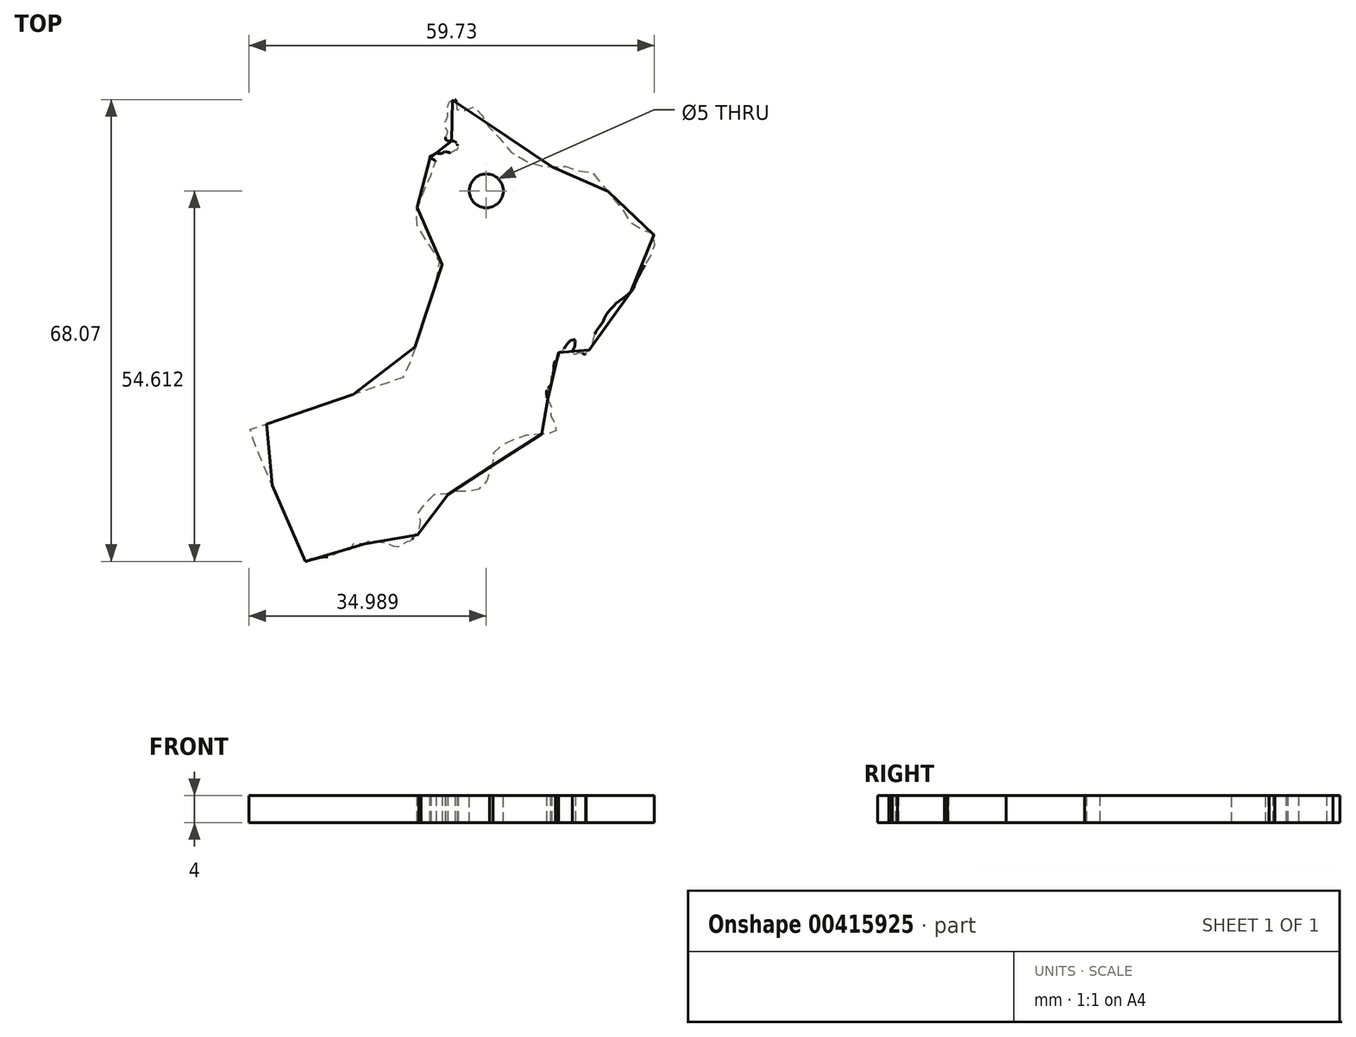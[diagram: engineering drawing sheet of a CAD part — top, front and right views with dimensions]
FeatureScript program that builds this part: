
annotation { "Feature Type Name" : "Feature", "Feature Type Description" : "" }
export const myFeature = defineFeature(function(context is Context, id is Id, definition is map)
    precondition{}
    {
        {
            var Q0;
            Q0=qCreatedBy(makeId("Top.planeOp"),FACE);
            var sketch = newSketch(context, id + "F0", { "sketchPlane" : qUnion([Q0])});
            skLineSegment(sketch, "E0", {"start": v(29.6, 33.78) * mm, "end": v(-30.4, -34.67) * mm, "construction": true});
            skPoint(sketch, "E1.287.internal.snap0", {"position": v(-0.4, -34.67) * mm});
            skFitSpline(sketch, "E1", {"points": [v(-21.86, -34.42) * mm, v(-22.26, -33.64) * mm, v(-22.63, -32.67) * mm, v(-23.08, -31.68) * mm, v(-23.6, -30.58) * mm, v(-23.98, -29.63) * mm, v(-24.43, -28.6) * mm, v(-24.98, -27.36) * mm, v(-25.63, -25.87) * mm, v(-25.94, -25.15) * mm, v(-26.4, -24.13) * mm, v(-26.85, -23.03) * mm, v(-27.5, -21.52) * mm, v(-27.88, -20.6) * mm, v(-28.48, -19.3) * mm, v(-28.76, -18.7) * mm, v(-29.17, -17.66) * mm, v(-29.58, -16.67) * mm, v(-29.95, -15.84) * mm, v(-30.23, -15.24) * mm, v(-30.16, -15.04) * mm, v(-29.37, -14.8) * mm, v(-28.12, -14.41) * mm, v(-27.2, -14.05) * mm, v(-25.85, -13.6) * mm, v(-25.24, -13.39) * mm, v(-23.99, -12.96) * mm, v(-23.02, -12.68) * mm, v(-21.7, -12.18) * mm, v(-20.03, -11.61) * mm, v(-18.68, -11.14) * mm, v(-17.36, -10.67) * mm, v(-15.5, -10.04) * mm, v(-14.32, -9.6) * mm, v(-12.78, -9.1) * mm, v(-11.22, -8.54) * mm, v(-10.12, -8.17) * mm, v(-8.72, -7.66) * mm, v(-7.5, -7.3) * mm, v(-7.05, -7.07) * mm, v(-6.8, -6.26) * mm, v(-6.51, -5.37) * mm, v(-6.2, -4.43) * mm, v(-5.8, -3) * mm, v(-5.36, -1.8) * mm, v(-4.98, -0.7) * mm, v(-4.86, -0.22) * mm, v(-4.67, 0.33) * mm, v(-4.07, 2.12) * mm, v(-3.53, 3.76) * mm, v(-3.2, 5) * mm, v(-2.82, 6.07) * mm, v(-2.13, 8.22) * mm, v(-1.83, 8.96) * mm, v(-1.76, 9.23) * mm, v(-2.13, 9.8) * mm, v(-2.7, 10.65) * mm, v(-3.13, 11.43) * mm, v(-3.7, 12.28) * mm, v(-4.33, 13.34) * mm, v(-4.88, 14.22) * mm, v(-5.22, 14.71) * mm, v(-5.38, 14.97) * mm, v(-5.45, 15.12) * mm, v(-5.4, 15.46) * mm, v(-5.3, 15.82) * mm, v(-5.3, 16.24) * mm, v(-5.43, 16.86) * mm, v(-5.5, 17.37) * mm, v(-5.46, 17.79) * mm, v(-5.27, 18.2) * mm, v(-4.83, 19.23) * mm, v(-4.5, 19.95) * mm, v(-3.97, 21.17) * mm, v(-3.8, 21.54) * mm, v(-3.52, 21.87) * mm, v(-3.39, 22.08) * mm, v(-3.43, 22.45) * mm, v(-3.35, 22.74) * mm, v(-3.17, 23.03) * mm, v(-2.82, 23.59) * mm, v(-2.67, 24.03) * mm, v(-2.67, 24.36) * mm, v(-2.8, 24.66) * mm, v(-3.11, 24.83) * mm, v(-3.5, 25) * mm, v(-3.6, 25.07) * mm, v(-3.53, 25.25) * mm, v(-3.18, 25.43) * mm, v(-2.68, 25.68) * mm, v(-2.23, 25.71) * mm, v(-1.86, 25.7) * mm, v(-1.63, 25.8) * mm, v(-1.4, 25.96) * mm, v(-1.1, 25.93) * mm, v(-0.76, 25.85) * mm, v(-0.5, 25.81) * mm, v(-0.17, 26) * mm, v(0.16, 26.18) * mm, v(0.3, 26.24) * mm, v(0.45, 26.29) * mm, v(0.56, 26.4) * mm, v(0.58, 26.62) * mm, v(0.48, 26.97) * mm, v(0.3, 27.34) * mm, v(0.12, 27.45) * mm, v(-0.15, 27.53) * mm, v(-0.5, 27.53) * mm, v(-0.99, 27.57) * mm, v(-1.25, 27.76) * mm, v(-1.25, 28.06) * mm, v(-1.1, 28.37) * mm, v(-0.94, 28.73) * mm, v(-1, 29.04) * mm, v(-1.19, 29.37) * mm, v(-1.28, 29.62) * mm, v(-1.34, 29.96) * mm, v(-1.27, 30.41) * mm, v(-1.07, 30.77) * mm, v(-0.96, 31.06) * mm, v(-0.94, 31.29) * mm, v(-0.94, 31.82) * mm, v(-0.91, 32.42) * mm, v(-0.81, 33.02) * mm, v(-0.56, 33.36) * mm, v(-0.22, 33.55) * mm, v(0.13, 33.63) * mm, v(0.35, 33.39) * mm, v(0.43, 33.12) * mm, v(0.23, 32.9) * mm, v(0.18, 32.5) * mm, v(0.48, 32.08) * mm, v(0.84, 31.76) * mm, v(1.2, 31.68) * mm, v(1.59, 32.05) * mm, v(2.04, 32.47) * mm, v(2.4, 32.5) * mm, v(2.79, 32.52) * mm, v(3.1, 32.62) * mm, v(3.59, 32.17) * mm, v(4.06, 31.42) * mm, v(4.48, 30.7) * mm, v(4.87, 29.95) * mm, v(5.4, 29.3) * mm, v(6.1, 28.54) * mm, v(6.78, 27.84) * mm, v(7.9, 26.45) * mm, v(8.72, 25.57) * mm, v(9.9, 24.86) * mm, v(11.58, 24.16) * mm, v(12.33, 23.89) * mm, v(13.5, 23.85) * mm, v(14.13, 23.82) * mm, v(14.6, 23.72) * mm, v(15.2, 23.85) * mm, v(15.72, 24.02) * mm, v(16.46, 23.79) * mm, v(17.25, 23.32) * mm, v(17.72, 23.05) * mm, v(18.52, 23.22) * mm, v(19.25, 23.19) * mm, v(20.52, 22.85) * mm, v(21.28, 22.12) * mm, v(21.48, 21.56) * mm, v(21.68, 21.1) * mm, v(22.35, 20.36) * mm, v(22.63, 20.13) * mm, v(22.96, 19.66) * mm, v(23.4, 19.09) * mm, v(23.94, 18.46) * mm, v(24.2, 18.08) * mm, v(24.7, 17.54) * mm, v(25.09, 17) * mm, v(25.48, 16.38) * mm, v(25.82, 15.8) * mm, v(26.45, 14.99) * mm, v(27.13, 14.55) * mm, v(28.3, 14.34) * mm, v(29, 14.22) * mm, v(29.34, 14) * mm, v(29.44, 13.45) * mm, v(29.48, 12.52) * mm, v(29.49, 12.2) * mm, v(29.46, 11.74) * mm, v(29.23, 11.22) * mm, v(28.97, 10.72) * mm, v(28.72, 10.37) * mm, v(28.43, 10.04) * mm, v(28.22, 9.5) * mm, v(27.94, 8.94) * mm, v(27.65, 8.49) * mm, v(27.25, 7.76) * mm, v(26.9, 7.06) * mm, v(26.48, 5.98) * mm, v(26.08, 5.33) * mm, v(25.45, 4.78) * mm, v(24.6, 4.14) * mm, v(23.97, 3.73) * mm, v(23.3, 3.01) * mm, v(22.66, 2.31) * mm, v(22.22, 1.6) * mm, v(21.9, 0.84) * mm, v(21.56, 0.43) * mm, v(21.01, -0.37) * mm, v(20.6, -1.27) * mm, v(20.36, -2.23) * mm, v(20.1, -2.99) * mm, v(19.7, -3.46) * mm, v(19.4, -3.72) * mm, v(19.42, -3.95) * mm, v(18.97, -3.81) * mm, v(18.5, -3.7) * mm, v(18.03, -3.83) * mm, v(17.65, -3.88) * mm, v(17.41, -3.65) * mm, v(17.56, -3.18) * mm, v(17.72, -2.8) * mm, v(17.8, -1.76) * mm, v(17.46, -1.79) * mm, v(16.97, -2.02) * mm, v(16.43, -2.68) * mm, v(16.03, -3.27) * mm, v(15.58, -3.55) * mm, v(15.44, -3.6) * mm, v(15.4, -4) * mm, v(15.41, -4.19) * mm, v(15.28, -4.47) * mm, v(14.97, -4.78) * mm, v(14.77, -5.12) * mm, v(14.7, -5.63) * mm, v(14.7, -6.21) * mm, v(14.6, -6.58) * mm, v(14.4, -6.98) * mm, v(14.26, -7.26) * mm, v(14.26, -7.6) * mm, v(14.26, -8.1) * mm, v(14.1, -8.5) * mm, v(13.86, -8.86) * mm, v(13.63, -9.3) * mm, v(13.6, -9.68) * mm, v(13.63, -9.93) * mm, v(13.72, -10.36) * mm, v(13.93, -10.8) * mm, v(14.1, -11.27) * mm, v(14.29, -11.63) * mm, v(14.35, -12.02) * mm, v(14.33, -12.52) * mm, v(14.22, -12.98) * mm, v(14.2, -13.42) * mm, v(14.54, -13.81) * mm, v(14.79, -14.03) * mm, v(14.97, -14.27) * mm, v(14.93, -14.62) * mm, v(14.93, -14.93) * mm, v(15, -15.13) * mm, v(15.04, -15.36) * mm, v(14.84, -15.51) * mm, v(14.41, -15.53) * mm, v(13.8, -15.58) * mm, v(13.08, -15.66) * mm, v(12.27, -15.73) * mm, v(11.54, -15.77) * mm, v(10.91, -15.83) * mm, v(10.3, -15.95) * mm, v(9.34, -16.28) * mm, v(8.45, -16.62) * mm, v(7.64, -16.95) * mm, v(6.95, -17.35) * mm, v(6.26, -17.92) * mm, v(5.88, -18.34) * mm, v(5.73, -18.73) * mm, v(5.72, -19.44) * mm, v(5.69, -19.98) * mm, v(5.5, -20.46) * mm, v(5.23, -20.84) * mm, v(5.19, -21.31) * mm, v(5.2, -21.85) * mm, v(5.12, -22.25) * mm, v(4.97, -22.41) * mm, v(4.5, -22.96) * mm, v(4.03, -23.44) * mm, v(3.48, -23.88) * mm, v(2.92, -24.17) * mm, v(2.23, -24.14) * mm, v(1.62, -24.1) * mm, v(0.88, -24.01) * mm, v(0.25, -24.2) * mm, v(-0.4, -24.57) * mm, v(-0.96, -24.54) * mm, v(-1.78, -24.44) * mm, v(-2.63, -24.51) * mm, v(-3.29, -24.78) * mm, v(-4.1, -25.53) * mm, v(-4.5, -26.2) * mm, v(-4.86, -26.7) * mm, v(-5.21, -27.1) * mm, v(-5.4, -27.65) * mm, v(-5.43, -28.05) * mm, v(-5.1, -28.36) * mm, v(-4.9, -28.73) * mm, v(-4.98, -29.2) * mm, v(-5.2, -29.46) * mm, v(-5.21, -30.12) * mm, v(-5.6, -30.82) * mm, v(-5.98, -31) * mm, v(-6.35, -31.25) * mm, v(-6.58, -31.52) * mm, v(-6.93, -31.55) * mm, v(-7.3, -31.73) * mm, v(-7.58, -31.98) * mm, v(-8.15, -32.26) * mm, v(-8.75, -32.26) * mm, v(-9.35, -32.05) * mm, v(-10.07, -31.77) * mm, v(-10.86, -31.62) * mm, v(-11.67, -31.48) * mm, v(-12.38, -31.43) * mm, v(-12.82, -31.59) * mm, v(-13.17, -31.84) * mm, v(-13.9, -31.82) * mm, v(-14.58, -31.78) * mm, v(-15.04, -32.01) * mm, v(-15.16, -32.53) * mm, v(-15.6, -32.76) * mm, v(-16.4, -32.76) * mm, v(-17, -33) * mm, v(-17.7, -33.46) * mm, v(-18.43, -33.72) * mm, v(-19.36, -33.8) * mm, v(-20.32, -34) * mm, v(-21.01, -34.14) * mm, v(-21.52, -34.33) * mm, v(-21.86, -34.42) * mm]});
            skSolve(sketch);
        }
        {
            var Q0;
            Q0=makeQuery(id+"F0.imprint","IMPRINT",FACE,{"disambiguationData":[TD([[makeQuery(id+"F0.imprint","IMPRINT",EDGE,{"derivedFrom":sQuery(id+"F0.wireOp",EDGE,"E1")}),-1.0]])]});
            extrude(context, id + "F1", {"entities" : qUnion([Q0]), "depth" : 4 * mm});
        }
        {
            var Q0;
            Q0=makeQuery(id+"F1.opExtrude","CAP_FACE",FACE,{"disambiguationData":[OSD([sQuery(id+"F0.wireOp",EDGE,"E1")])],"isStart":false});
            var sketch = newSketch(context, id + "F2", { "sketchPlane" : qUnion([Q0])});
            skCircle(sketch, "E2", {"center": v(4.75, 20.18) * mm, "radius": 2.5 * mm});
            skSolve(sketch);
        }
        {
            var Q0;
            Q0=makeQuery(id+"F2.imprint","IMPRINT",FACE,{"disambiguationData":[TD([[makeQuery(id+"F2.imprint","IMPRINT",EDGE,{"derivedFrom":sQuery(id+"F2.wireOp",EDGE,"E2")}),1.0]])]});
            extrude(context, id + "F3", {"entities" : qUnion([Q0]), "operationType" : NewBodyOperationType.REMOVE, "oppositeDirection" : true, "depth" : 25 * mm});
        }
    });
